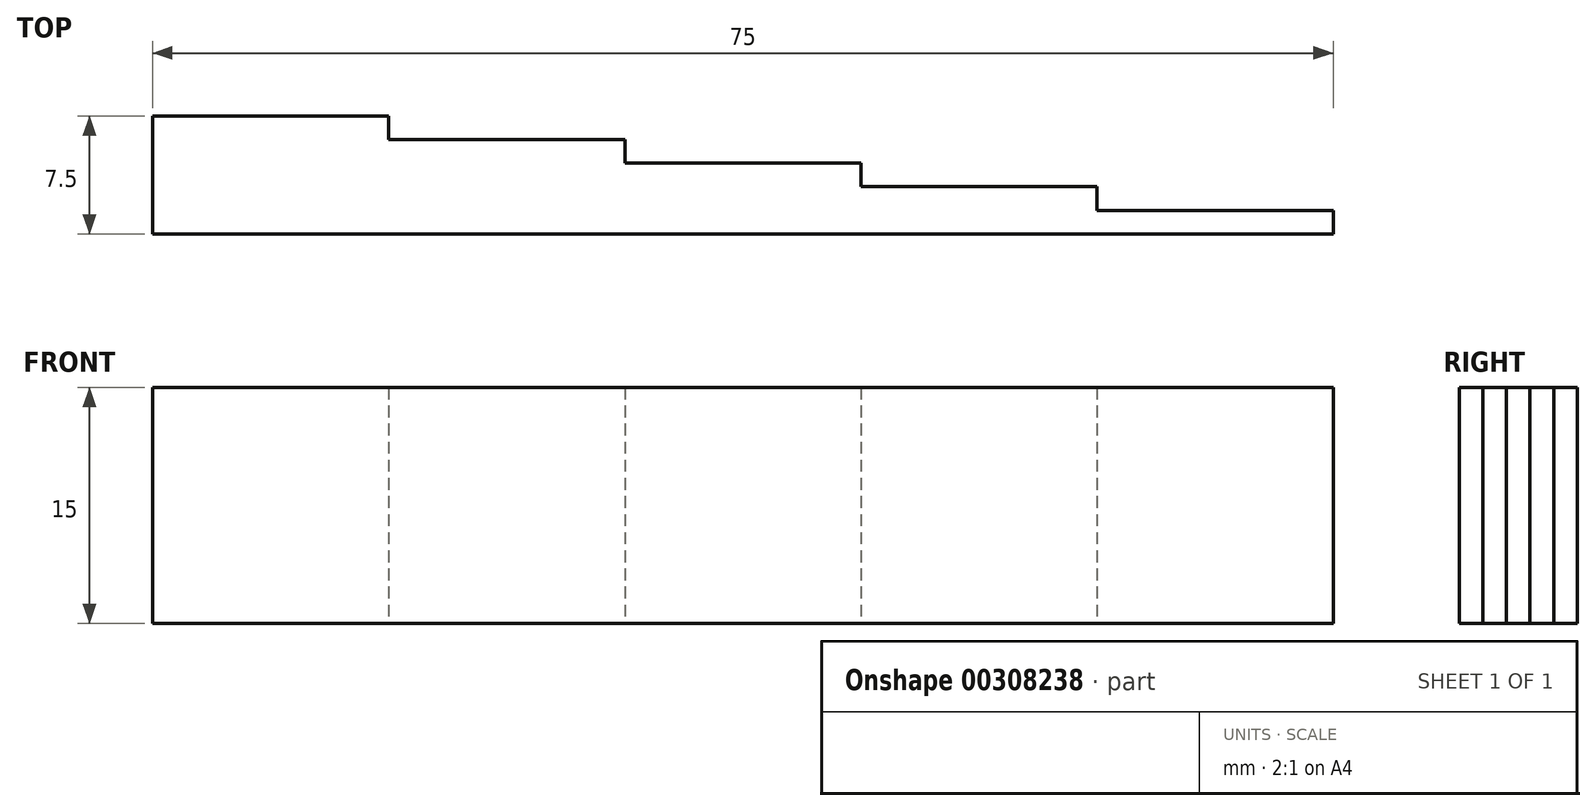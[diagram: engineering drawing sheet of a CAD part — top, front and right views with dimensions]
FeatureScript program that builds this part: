
annotation { "Feature Type Name" : "Feature", "Feature Type Description" : "" }
export const myFeature = defineFeature(function(context is Context, id is Id, definition is map)
    precondition{}
    {
        {
            var Q0;
            Q0=qCreatedBy(makeId("Top.planeOp"),FACE);
            var sketch = newSketch(context, id + "F0", { "sketchPlane" : qUnion([Q0])});
            skLineSegment(sketch, "E0", {"start": v(-34.34, 9.34) * mm, "end": v(-19.34, 9.34) * mm});
            skLineSegment(sketch, "E1", {"start": v(-19.34, 9.34) * mm, "end": v(-19.34, 7.84) * mm});
            skLineSegment(sketch, "E2", {"start": v(-19.34, 7.84) * mm, "end": v(-4.34, 7.84) * mm});
            skLineSegment(sketch, "E3", {"start": v(-4.34, 7.84) * mm, "end": v(-4.34, 6.34) * mm});
            skLineSegment(sketch, "E4", {"start": v(-4.34, 6.34) * mm, "end": v(10.66, 6.34) * mm});
            skLineSegment(sketch, "E5", {"start": v(10.66, 6.34) * mm, "end": v(10.66, 4.84) * mm});
            skLineSegment(sketch, "E6", {"start": v(10.66, 4.84) * mm, "end": v(25.66, 4.84) * mm});
            skLineSegment(sketch, "E7", {"start": v(25.66, 4.84) * mm, "end": v(25.66, 3.34) * mm});
            skLineSegment(sketch, "E8", {"start": v(25.66, 3.34) * mm, "end": v(40.66, 3.34) * mm});
            skLineSegment(sketch, "E9", {"start": v(40.66, 3.34) * mm, "end": v(40.66, 1.84) * mm});
            skLineSegment(sketch, "E10", {"start": v(40.66, 1.84) * mm, "end": v(-34.34, 1.84) * mm});
            skLineSegment(sketch, "E11", {"start": v(-34.34, 1.84) * mm, "end": v(-34.34, 9.34) * mm});
            skSolve(sketch);
        }
        {
            var Q0;
            Q0=makeQuery(id+"F0.imprint","IMPRINT",FACE,{"disambiguationData":[TD([[makeQuery(id+"F0.imprint","IMPRINT",EDGE,{"derivedFrom":sQuery(id+"F0.wireOp",EDGE,"E0")}),-1.0]])]});
            extrude(context, id + "F1", {"entities" : qUnion([Q0]), "depth" : 15 * mm, "offsetDistance" : 25 * mm});
        }
    });
